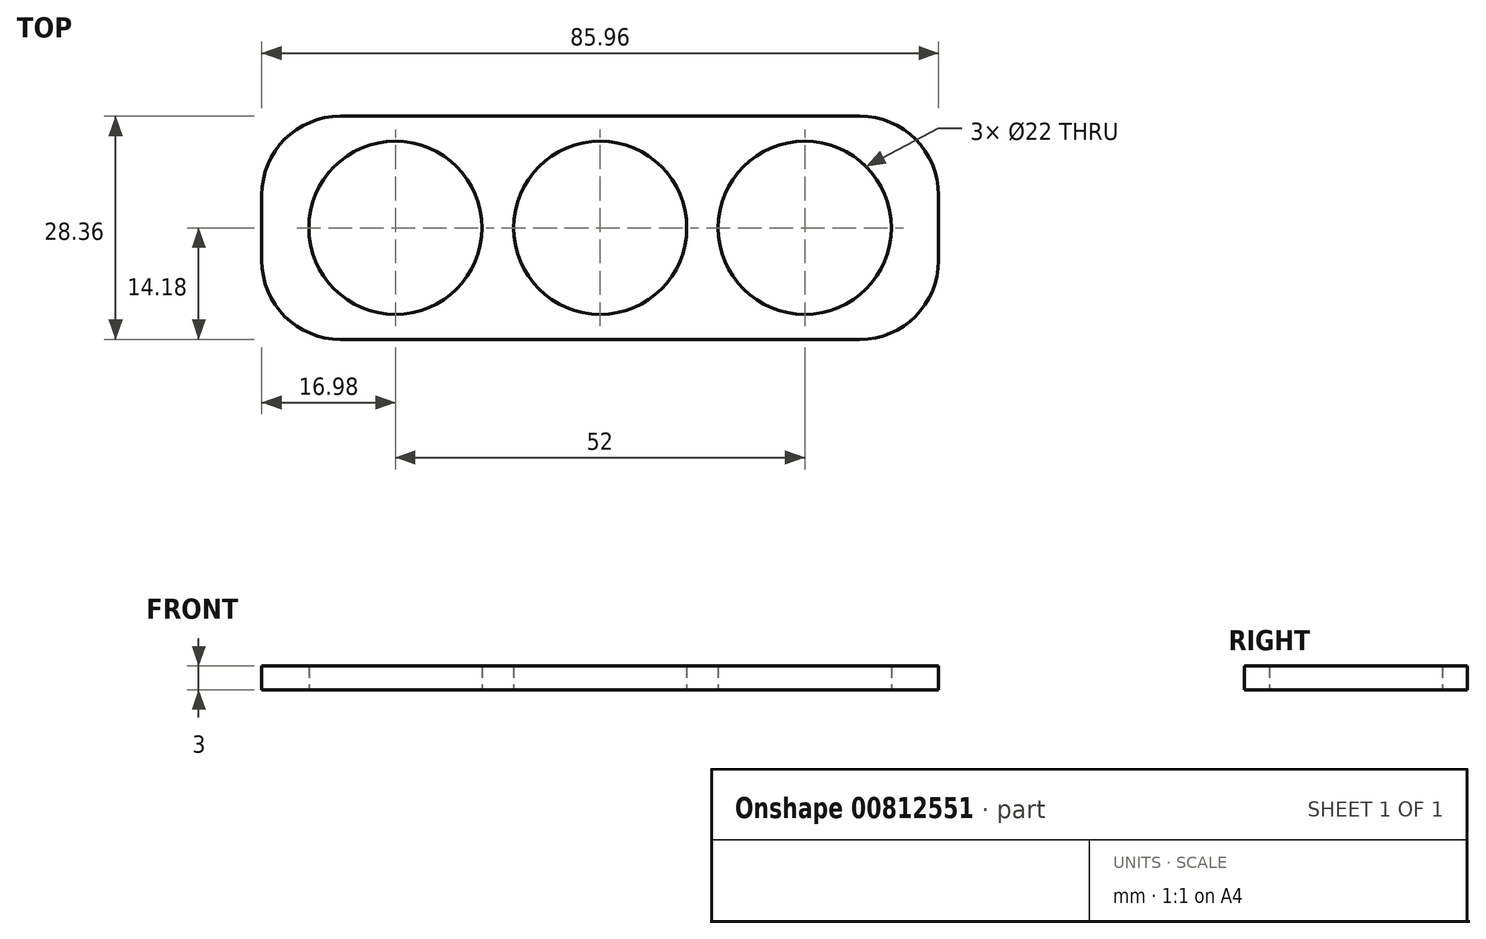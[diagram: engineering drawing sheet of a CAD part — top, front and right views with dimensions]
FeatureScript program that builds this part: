
annotation { "Feature Type Name" : "Feature", "Feature Type Description" : "" }
export const myFeature = defineFeature(function(context is Context, id is Id, definition is map)
    precondition{}
    {
        {
            var Q0;
            Q0=qCreatedBy(makeId("Top.planeOp"),FACE);
            var sketch = newSketch(context, id + "F0", { "sketchPlane" : qUnion([Q0])});
            skCircle(sketch, "E0", {"center": v(0, 0) * mm, "radius": 11 * mm});
            skCircle(sketch, "E1", {"center": v(26, 0) * mm, "radius": 11 * mm});
            skCircle(sketch, "E2", {"center": v(-26, 0) * mm, "radius": 11 * mm});
            skLineSegment(sketch, "E3.bottom", {"start": v(-32.98, 14.18) * mm, "end": v(32.98, 14.18) * mm});
            skLineSegment(sketch, "E3.top", {"start": v(-32.98, -14.18) * mm, "end": v(32.98, -14.18) * mm});
            skLineSegment(sketch, "E3.left", {"start": v(-42.98, 4.18) * mm, "end": v(-42.98, -4.18) * mm});
            skLineSegment(sketch, "E3.right", {"start": v(42.98, 4.18) * mm, "end": v(42.98, -4.18) * mm});
            skPoint(sketch, "E4.visualSharp", {"position": v(42.98, 14.18) * mm});
            skArc(sketch, "E4.filletArc", {"start": v(42.98, 4.18) * mm, "mid": v(40.05, 11.25) * mm, "end": v(32.98, 14.18) * mm});
            skPoint(sketch, "E5.visualSharp", {"position": v(42.98, -14.18) * mm});
            skArc(sketch, "E5.filletArc", {"start": v(32.98, -14.18) * mm, "mid": v(40.05, -11.25) * mm, "end": v(42.98, -4.18) * mm});
            skPoint(sketch, "E6.visualSharp", {"position": v(-42.98, -14.18) * mm});
            skArc(sketch, "E6.filletArc", {"start": v(-42.98, -4.18) * mm, "mid": v(-40.05, -11.25) * mm, "end": v(-32.98, -14.18) * mm});
            skPoint(sketch, "E7.visualSharp", {"position": v(-42.98, 14.18) * mm});
            skArc(sketch, "E7.filletArc", {"start": v(-32.98, 14.18) * mm, "mid": v(-40.05, 11.25) * mm, "end": v(-42.98, 4.18) * mm});
            skSolve(sketch);
        }
        {
            var Q0;
            Q0=makeQuery(id+"F0.imprint","IMPRINT",FACE,{"disambiguationData":[TD([[makeQuery(id+"F0.imprint","IMPRINT",EDGE,{"derivedFrom":sQuery(id+"F0.wireOp",EDGE,"E1")}),-1.0]])]});
            extrude(context, id + "F1", {"entities" : qUnion([Q0]), "depth" : 3 * mm, "offsetDistance" : 25 * mm});
        }
    });
